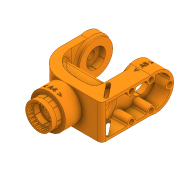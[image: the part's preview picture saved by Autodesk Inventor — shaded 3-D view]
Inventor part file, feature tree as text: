
AUTODESK INVENTOR PART (.ipt)
format: ipt  version: 2020 (Build 240168000, 168)  size: 2,109,440 bytes
history: native  units: in
note: dims shown in document units (in); Inventor stores cm internally (conversion verified against a paired STEP export)
features: sketch x41, extrude x37, projected_geometry x29, chamfer x8, fillet x8, plane x6, emboss x3
ambient origin geometry x8: Origin, YZ Plane, XZ Plane, XY Plane, X Axis, Y Axis, Z Axis, Center Point
bodies: Solid1 (feature_tree)
feature tree (132):
  extrude  "Extrusion1"  Depth=2.0472in
  extrude  "Extrusion2"  Depth=1.1063in
  chamfer  "Chamfer2"  Distance=0.2756in
  extrude  "Extrusion4"  Depth=0.0157in
  extrude  "Extrusion7"  Depth=0.2756in TaperAngle=0.0deg
  chamfer  "Chamfer4"  Distance=0.0394in
  extrude  "Extrusion8"  Depth=0.0157in
  sketch  "Sketch12"  dims[d39=1.4567in d57=0.0394in d58=0.0in]
  plane  "Work Plane1"
  sketch  "Sketch13"  dims[d59=0.315in d60=0.125in d61=0.0137in d67=0.0157in]
  extrude  "Extrusion10"  Depth=0.0394in TaperAngle=0.0deg
  extrude  "Extrusion11"  Depth=0.0866in
  chamfer  "Chamfer5"  Distance=9.4488in Angle=360.0deg
  extrude  "Extrusion12"  Depth=0.2756in TaperAngle=0.0deg
  plane  "Work Plane2"
  extrude  "Extrusion13"  Depth=0.315in
  plane  "Work Plane3"
  extrude  "Extrusion14"  Depth=1.0236in
  extrude  "Extrusion15"  Depth=0.8858in
  extrude  "Extrusion16"  Depth=0.3937in
  extrude  "Extrusion17"  Depth=1.378in
  sketch  "Sketch21"  dims[d107=0.315in d108=0.0in d109=0.315in d110=0.125in d111=0.0137in]
  extrude  "Extrusion19"  Depth=0.5906in
  sketch  "Sketch23"  dims[d112=1.0in d113=0.0in d114=1.0236in]
  extrude  "Extrusion20"  Depth=0.1575in TaperAngle=0.0deg
  extrude  "Extrusion21"  Depth=0.1575in TaperAngle=0.0deg
  extrude  "Extrusion22"  Depth=4.2323in
  extrude  "Extrusion23"  Depth=0.1575in
  extrude  "Extrusion24"  Depth=1.1024in
  extrude  "Extrusion25"  Depth=0.4921in
  extrude  "Extrusion26"  Depth=0.75in
  extrude  "Extrusion27"  Depth=0.2165in TaperAngle=0.0deg
  extrude  "Extrusion28"  Depth=0.1575in
  extrude  "Extrusion29"  Depth=1.1811in
  plane  "Work Plane4"
  extrude  "Extrusion30"  Depth=0.3937in TaperAngle=0.0deg
  fillet  "Fillet1"  Radius=0.3937in
  fillet  "Fillet2"  Radius=0.315in
  extrude  "Extrusion31"  Depth=0.315in TaperAngle=0.0deg
  extrude  "Extrusion32"  Depth=0.315in TaperAngle=0.0deg
  extrude  "Extrusion33"  Depth=0.3937in TaperAngle=0.0deg
  fillet  "Fillet3"  Radius=0.2165in
  extrude  "Extrusion34"  Depth=0.4724in
  chamfer  "Chamfer6"  Distance=0.2756in
  chamfer  "Chamfer7"  Distance=0.0394in
  extrude  "Extrusion35"  Depth=0.001in
  extrude  "Extrusion36"  Depth=1.0in TaperAngle=0.0deg
  fillet  "Fillet5"  Radius=0.1575in
  extrude  "Extrusion38"  Depth=0.315in
  extrude  "Extrusion39"  Depth=0.1969in
  extrude  "Extrusion40"  Depth=0.1969in TaperAngle=360.0deg
  fillet  "Fillet7"  Radius=1.0in
  extrude  "Extrusion41"  Depth=0.1969in TaperAngle=0.0deg
  chamfer  "Chamfer8"  Distance=0.1969in
  extrude  "Extrusion42"  Depth=0.3937in TaperAngle=0.0deg
  plane  "Work Plane6"
  emboss  "Emboss1"
  emboss  "Emboss2"
  plane  "Work Plane7"
  emboss  "Emboss3"
  extrude  "Extrusion43"  Depth=0.1969in
  fillet  "Fillet9"  Radius=0.0787in
  fillet  "Fillet10"  Radius=0.1969in
  chamfer  "Chamfer9"  Distance=0.1181in
  fillet  "Fillet11"  Radius=1.0039in
  chamfer  "Chamfer10"  Distance=0.4134in
  sketch  "Sketch1"  dims[d0=0.6299in d1=2.0472in]
  sketch  "Sketch2"  dims[d2=0.9449in d3=0.0in d4=1.1063in]
  sketch  "Sketch4"  dims[d5=1.5748in d6=0.2756in d7=0.0in]
  sketch  "Sketch8"  dims[d11=0.2756in d12=0.125in d13=0.0137in d25=0.0157in]
  projected_geometry  "Projected Loop2"
  sketch  "Sketch10"  dims[d26=6.2992in d28=360.0deg d30=0.2756in d31=0.0in]
  sketch  "Sketch14"  dims[d68=4.7244in d70=360.0deg d72=0.0394in d73=0.0in]
  sketch  "Sketch15"  dims[d83=0.0591in d84=0.0866in]
  projected_geometry  "Projected Loop4"
  sketch  "Sketch16"  dims[d85=0.0827in]
  sketch  "Sketch17"  dims[d86=0.0827in]
  projected_geometry  "Projected Loop5"
  sketch  "Sketch18"  dims[d87=0.0827in d88=9.4488in d90=360.0deg]
  projected_geometry  "Projected Loop6"
  projected_geometry  "Projected Loop7"
  sketch  "Sketch19"  dims[d92=0.2756in]
  projected_geometry  "Projected Loop8"
  projected_geometry  "Projected Loop9"
  sketch  "Sketch20"  dims[d94=9.4488in d95=0.0827in d96=0.0827in d97=0.0827in d98=360.0deg d105=0.2756in d106=0.0in]
  projected_geometry  "Projected Loop10"
  projected_geometry  "Projected Loop11"
  projected_geometry  "Projected Loop12"
  projected_geometry  "Projected Loop13"
  sketch  "Sketch25"  dims[d115=0.7874in d117=0.8858in]
  sketch  "Sketch26"  dims[d118=2.7559in d119=0.3937in]
  projected_geometry  "Projected Loop16"
  projected_geometry  "Projected Loop17"
  sketch  "Sketch27"  dims[d120=0.5906in d121=1.378in]
  projected_geometry  "Projected Loop18"
  projected_geometry  "Projected Loop19"
  sketch  "Sketch28"  dims[d123=3.4941in d124=0.5906in]
  projected_geometry  "Projected Loop20"
  projected_geometry  "Projected Loop21"
  sketch  "Sketch29"  dims[d126=1.9685in d129=0.1575in d130=0.0in]
  projected_geometry  "Projected Loop22"
  projected_geometry  "Projected Loop23"
  sketch  "Sketch30"  dims[d131=-2.0472in d132=0.1575in d133=0.0in]
  projected_geometry  "Projected Loop24"
  sketch  "Sketch31"  dims[d134=2.126in d136=4.2323in]
  sketch  "Sketch32"  dims[d137=0.1575in d138=0.1575in]
  sketch  "Sketch34"  dims[d139=0.4921in d140=0.0in d141=1.1024in]
  projected_geometry  "Projected Loop25"
  sketch  "Sketch35"  dims[d142=1.1614in d143=0.4921in]
  sketch  "Sketch36"  dims[d144=0.3445in d145=0.75in]
  projected_geometry  "Projected Loop26"
  sketch  "Sketch37"  dims[d146=0.1575in d147=0.0in d148=0.2165in d149=0.0in]
  projected_geometry  "Projected Loop27"
  sketch  "Sketch38"  dims[d152=1.0039in d153=0.0in d154=0.1575in]
  projected_geometry  "Projected Loop28"
  sketch  "Sketch39"  dims[d155=0.1575in d160=1.1811in]
  projected_geometry  "Projected Loop29"
  sketch  "Sketch40"  dims[d161=0.1969in d162=0.0in d163=0.315in d164=0.0in d165=0.3937in d166=0.0in d167=0.315in d168=0.0in]
  sketch  "Sketch41"  dims[d169=0.315in d170=0.0in d171=0.315in d172=0.0in]
  projected_geometry  "Projected Loop30"
  sketch  "Sketch43"  dims[d173=0.315in d174=0.0in d175=0.315in d176=0.0in]
  projected_geometry  "Projected Loop31"
  sketch  "Sketch44"  dims[d177=1.1024in d178=0.3937in d179=0.0in d180=0.2165in d181=0.0in]
  sketch  "Sketch45"  dims[d183=-0.0197in d184=0.4724in d185=0.2756in d186=0.0in]
  sketch  "Sketch46"  dims[d187=0.5512in]
  projected_geometry  "Projected Loop32"
  sketch  "Sketch47"  dims[d188=0.2165in d189=0.0394in d190=0.0in]
  projected_geometry  "Projected Loop33"
  sketch  "Sketch48"  dims[d191=0.0394in d192=0.0in d193=0.001in]
  sketch  "Sketch49"  dims[d194=0.001in d195=1.0in d196=0.0in d197=0.1575in]
  sketch  "Sketch50"  dims[d198=1.0in d199=0.0in d200=0.315in d201=0.125in d202=0.0137in]
  sketch  "Sketch52"  dims[d203=0.315in d204=0.125in d205=0.0137in d206=0.0157in d207=2.3622in d209=360.0deg d211=1.0in d212=0.0in d213=1.0in d214=0.0in d221=0.1969in d222=0.3937in d223=0.0in d224=0.1575in d225=0.0787in d226=0.1969in d227=0.0in d229=0.1181in d230=1.0039in d231=0.4134in d232=0.5118in d233=0.0984in d235=0.0197in d236=0.1181in d237=0.1181in d238=0.2047in d239=0.2047in d240=0.0in d241=0.0in d242=0.2362in d243=0.0787in d244=0.0787in d251=0.0787in d252=0.0787in d253=0.2756in d254=0.4724in d255=0.2756in d256=0.4724in d257=0.2756in d258=0.4724in d259=0.2756in d260=0.4724in d261=0.1575in d262=0.0in d263=0.0787in d264=0.125in d265=45.0deg d266=1.0in d267=0.0in d269=0.0394in d270=0.0in d271=0.0394in d272=0.0in d273=0.0394in d274=0.0in d275=0.0039in d276=0.0787in d277=1.0in d278=0.0in d279=0.122in d280=0.2264in d282=0.1378in d283=0.2047in d284=0.1575in d285=0.125in d286=45.0deg d287=0.1575in d288=0.0394in d289=0.125in d290=45.0deg]
